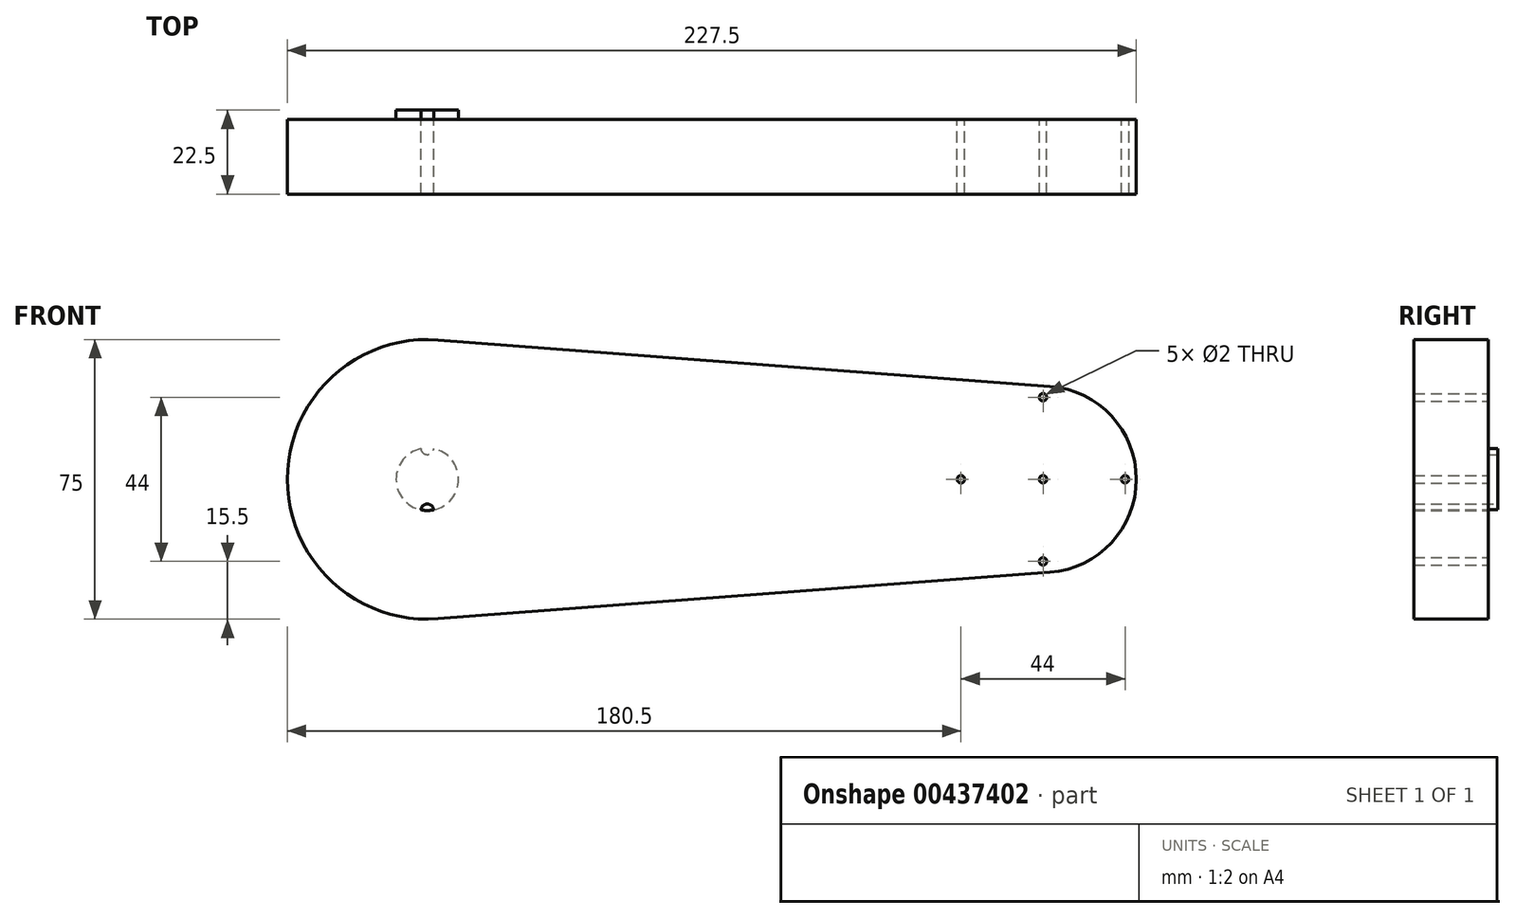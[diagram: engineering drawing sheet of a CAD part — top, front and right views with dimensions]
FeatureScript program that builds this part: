
annotation { "Feature Type Name" : "Feature", "Feature Type Description" : "" }
export const myFeature = defineFeature(function(context is Context, id is Id, definition is map)
    precondition{}
    {
        {
            var Q0;
            Q0=qCreatedBy(makeId("Front.planeOp"),FACE);
            var sketch = newSketch(context, id + "F0", { "sketchPlane" : qUnion([Q0])});
            skCircle(sketch, "E0", {"center": v(0, 0) * mm, "radius": 37.5 * mm});
            skCircle(sketch, "E1", {"center": v(165, 0) * mm, "radius": 25 * mm});
            skLineSegment(sketch, "E2", {"start": v(2.84, 37.4) * mm, "end": v(166.9, 24.93) * mm});
            skLineSegment(sketch, "E3", {"start": v(2.84, -37.4) * mm, "end": v(166.9, -24.93) * mm});
            skCircle(sketch, "E4", {"center": v(0, 0) * mm, "radius": 8.38 * mm});
            skCircle(sketch, "E5", {"center": v(165, 0) * mm, "radius": 1 * mm});
            skArc(sketch, "E6", {"start": v(0, 6.63) * mm, "mid": v(1.17, 7.07) * mm, "end": v(1.74, 8.2) * mm});
            skArc(sketch, "E7", {"start": v(0, 6.63) * mm, "mid": v(-1.17, 7.07) * mm, "end": v(-1.74, 8.2) * mm});
            skArc(sketch, "E8", {"start": v(0, -6.63) * mm, "mid": v(1.17, -7.07) * mm, "end": v(1.74, -8.2) * mm});
            skArc(sketch, "E9", {"start": v(0, -6.63) * mm, "mid": v(-1.17, -7.07) * mm, "end": v(-1.74, -8.2) * mm});
            skCircle(sketch, "E10", {"center": v(0, 0) * mm, "radius": 12.5 * mm});
            skCircle(sketch, "E11", {"center": v(165, 22) * mm, "radius": 1 * mm});
            skCircle(sketch, "E12", {"center": v(165, -22) * mm, "radius": 1 * mm});
            skCircle(sketch, "E13", {"center": v(187, 0) * mm, "radius": 1 * mm});
            skCircle(sketch, "E14", {"center": v(143, 0) * mm, "radius": 1 * mm});
            skSolve(sketch);
        }
        {
            var Q0;
            Q0=makeQuery(id+"F0.imprint","IMPRINT",FACE,{"disambiguationData":[TD([[makeQuery(id+"F0.imprint","IMPRINT",EDGE,{"derivedFrom":sQuery(id+"F0.wireOp",EDGE,"E10")}),-1.0]])]});
            var Q1;
            {var subQ0=sQuery(id+"F0.wireOp",EDGE,"E6");Q1=makeQuery(id+"F0.imprint","IMPRINT",FACE,{"disambiguationData":[TD([[makeQuery(id+"F0.imprint","IMPRINT",EDGE,{"derivedFrom":subQ0}),1.0]])]});}
            var Q2;
            {var subQ0=sQuery(id+"F0.wireOp",EDGE,"E8");Q2=makeQuery(id+"F0.imprint","IMPRINT",FACE,{"disambiguationData":[TD([[makeQuery(id+"F0.imprint","IMPRINT",EDGE,{"derivedFrom":subQ0}),-1.0]])]});}
            var Q3;
            Q3=makeQuery(id+"F0.imprint","IMPRINT",FACE,{"disambiguationData":[TD([[makeQuery(id+"F0.imprint","IMPRINT",EDGE,{"derivedFrom":sQuery(id+"F0.wireOp",EDGE,"E10")}),1.0]])]});
            var Q4;
            {var subQ0=sQuery(id+"F0.wireOp",EDGE,"E2");Q4=makeQuery(id+"F0.imprint","IMPRINT",FACE,{"disambiguationData":[TD([[makeQuery(id+"F0.imprint","IMPRINT",EDGE,{"derivedFrom":subQ0}),-1.0]])]});}
            var Q5;
            Q5=makeQuery(id+"F0.imprint","IMPRINT",FACE,{"disambiguationData":[TD([[makeQuery(id+"F0.imprint","IMPRINT",EDGE,{"derivedFrom":sQuery(id+"F0.wireOp",EDGE,"E5")}),-1.0]])]});
            extrude(context, id + "F1", {"entities" : qUnion([Q0, Q1, Q2, Q3, Q4, Q5]), "depth" : 20 * mm});
        }
        {
            var Q0;
            {var subQ0=sQuery(id+"F0.wireOp",EDGE,"E6");Q0=makeQuery(id+"F0.imprint","IMPRINT",FACE,{"disambiguationData":[TD([[makeQuery(id+"F0.imprint","IMPRINT",EDGE,{"derivedFrom":subQ0}),-1.0]])]});}
            extrude(context, id + "F2", {"entities" : qUnion([Q0]), "operationType" : NewBodyOperationType.ADD, "endBound" : BoundingType.SYMMETRIC, "depth" : 5 * mm});
        }
    });
